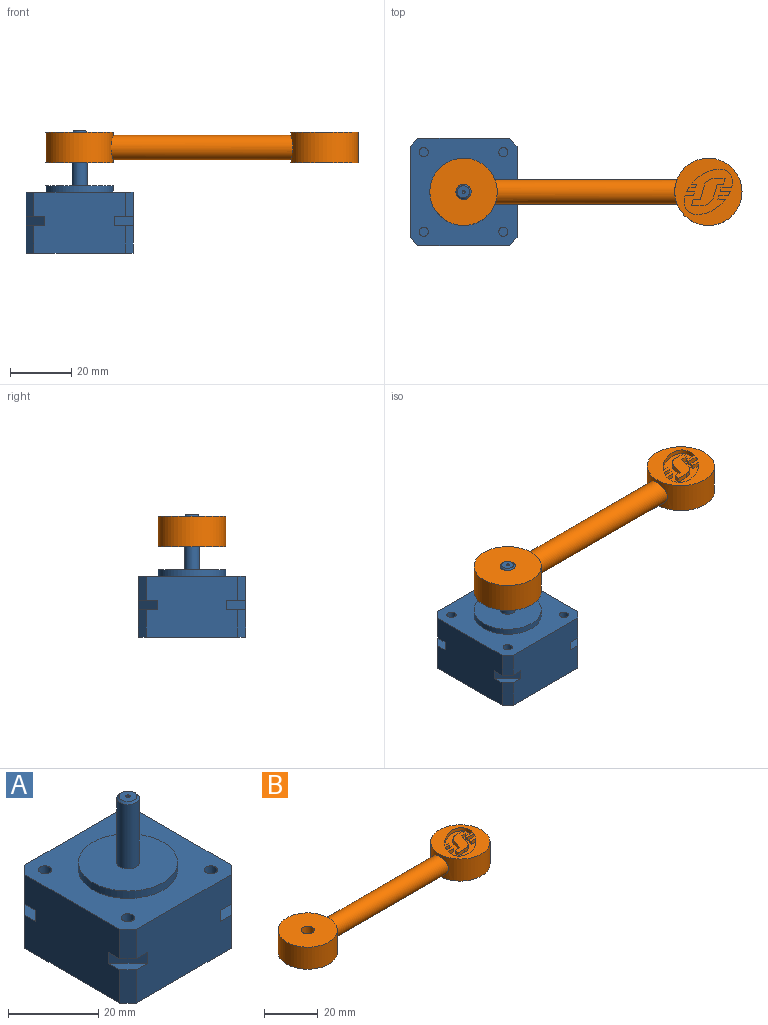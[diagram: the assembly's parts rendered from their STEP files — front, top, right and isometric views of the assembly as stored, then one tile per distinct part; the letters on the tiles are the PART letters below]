
ASSEMBLY  parts=2 mates=1
PART A: 41 faces, bbox 35x35x40 mm
  f0: plane 35x35mm, normal (0,0,1), area 803.1mm2, adj f1,f2,f3,f4,f13,f14,f15,f16
  f1: plane 29.8x20mm, normal (-1,0,0), area 575mm2, adj f0,f5,f8,f9,f10,f13,f16,f17
  f2: plane 29.8x20mm, normal (0,-1,0), area 575mm2, adj f0,f7,f8,f10,f11,f15,f16,f19
  f3: plane 29.8x20mm, normal (1,0,0), area 575mm2, adj f0,f6,f7,f11,f12,f14,f15,f18
  f4: plane 29.8x20mm, normal (0,1,0), area 575mm2, adj f0,f5,f6,f9,f12,f13,f14,f17
  f5: plane 6.1x6.1mm, normal (-0.71,0.71,0), area 25.9mm2, adj f1,f4,f9,f17
  f6: plane 6.1x6.1mm, normal (0.71,0.71,0), area 25.9mm2, adj f3,f4,f12,f18
  f7: plane 6.1x6.1mm, normal (0.71,-0.71,0), area 25.9mm2, adj f2,f3,f11,f19
  f8: plane 6.1x6.1mm, normal (-0.71,-0.71,0), area 25.9mm2, adj f1,f2,f10,f20
  f9: plane 6.1x6.1mm, normal (0,0,-1), area 15.2mm2, adj f1,f4,f5,f13
  f10: plane 6.1x6.1mm, normal (0,0,-1), area 15.2mm2, adj f1,f2,f8,f16
  f11: plane 6.1x6.1mm, normal (0,0,-1), area 15.2mm2, adj f2,f3,f7,f15
  f12: plane 6.1x6.1mm, normal (0,0,-1), area 15.2mm2, adj f3,f4,f6,f14
  f13: plane 8x2.6mm, normal (-0.71,0.71,0), area 29.4mm2, adj f0,f1,f4,f9
  f14: plane 8x2.6mm, normal (0.71,0.71,0), area 29.4mm2, adj f0,f3,f4,f12
  f15: plane 8x2.6mm, normal (0.71,-0.71,0), area 29.4mm2, adj f0,f2,f3,f11
  f16: plane 8x2.6mm, normal (-0.71,-0.71,0), area 29.4mm2, adj f0,f1,f2,f10
  f17: plane 6.1x6.1mm, normal (0,0,1), area 15.2mm2, adj f1,f4,f5,f23
  f18: plane 6.1x6.1mm, normal (0,0,1), area 15.2mm2, adj f3,f4,f6,f24
  f19: plane 6.1x6.1mm, normal (0,0,1), area 15.2mm2, adj f2,f3,f7,f21
  f20: plane 6.1x6.1mm, normal (0,0,1), area 15.2mm2, adj f1,f2,f8,f22
  f21: plane 9x2.6mm, normal (0.71,-0.71,0), area 33.1mm2, adj f2,f3,f19,f25
  f22: plane 9x2.6mm, normal (-0.71,-0.71,0), area 33.1mm2, adj f1,f2,f20,f25
  f23: plane 9x2.6mm, normal (-0.71,0.71,0), area 33.1mm2, adj f1,f4,f17,f25
  f24: plane 9x2.6mm, normal (0.71,0.71,0), area 33.1mm2, adj f3,f4,f18,f25
  f25: plane 35x35mm, normal (0,0,-1), area 1211.5mm2, adj f1,f2,f3,f4,f21,f22,f23,f24
  f26: cylinder r=11mm len=22mm, axis (0,0,-1), area 138.2mm2, adj f0,f27
  f27: plane 22x22mm, normal (0,0,1), area 360.5mm2, adj f26,f28
  f28: cylinder r=2.5mm len=17.5mm, axis (0,0,-1), area 274.9mm2, adj f27,f38
  f29: plane 4x4mm, normal (0,0,1), area 11.8mm2, adj f38,f39
  f30: cylinder r=1.5mm len=6mm, axis (0,0,1), area 56.5mm2, adj f0,f31
  f31: plane 3x3mm, normal (0,0,1), area 7.1mm2, adj f30
  f32: cylinder r=1.5mm len=6mm, axis (0,0,1), area 56.5mm2, adj f0,f33
  f33: plane 3x3mm, normal (0,0,1), area 7.1mm2, adj f32
  f34: cylinder r=1.5mm len=6mm, axis (0,0,1), area 56.5mm2, adj f0,f35
  f35: plane 3x3mm, normal (0,0,1), area 7.1mm2, adj f34
  f36: cylinder r=1.5mm len=6mm, axis (0,0,1), area 56.5mm2, adj f0,f37
  f37: plane 3x3mm, normal (0,0,1), area 7.1mm2, adj f36
  f38: cone r=2mm half-angle=45deg, axis (0,0,-1), area 10mm2, adj f28,f29
  f39: cylinder r=0.5mm len=3mm, axis (0,0,1), area 9.4mm2, adj f29,f40
  f40: cone r=0mm half-angle=59deg, axis (0,0,1), area 0.9mm2, adj f39
PART B: 36 faces, bbox 102x22x10 mm
  f0: extruded ~1.5x1.29mm, area 2.2mm2, adj f9,f13,f14,f24
  f1: extruded ~13.49x6.23mm, area 29.4mm2, adj f9,f16,f17,f24
  f2: extruded ~1.5x1.35mm, area 2.3mm2, adj f9,f19,f20,f24
  f3: extruded ~13.46x6.12mm, area 29.2mm2, adj f9,f22,f23,f24
  f4: cylinder r=11mm len=22mm, axis (0,0,-1), area 640.1mm2, adj f6,f7,f11
  f5: cylinder r=2.45mm len=10mm, axis (0,0,-1), area 153.9mm2, adj f6,f7
  f6: plane 22x22mm, normal (0,0,1), area 361.3mm2, adj f4,f5
  f7: plane 22x22mm, normal (0,0,-1), area 361.3mm2, adj f4,f5
  f8: cylinder r=11mm len=22mm, axis (0,0,-1), area 640.1mm2, adj f9,f10,f11
  f9: plane 22x22mm, normal (0,0,1), area 227.2mm2, adj f0,f1,f2,f3,f8,f12,f13,f14
  f10: plane 22x22mm, normal (0,0,-1), area 380.1mm2, adj f8
  f11: cylinder r=4mm len=59.51mm, axis (-1,0,0), area 1476.4mm2, adj f4,f8
  f12: plane 1.5x1.19mm, normal (0.97,-0.26,0), area 1.8mm2, adj f9,f13,f23,f24
  f13: plane 2.27x1.5mm, normal (0,-1,0), area 3.4mm2, adj f0,f9,f12,f24
  f14: plane 2.62x1.5mm, normal (0,1,0), area 3.9mm2, adj f0,f9,f15,f24
  f15: plane 1.5x1.19mm, normal (0.97,-0.26,0), area 1.8mm2, adj f9,f14,f16,f24
  f16: plane 2.75x1.5mm, normal (0,-1,0), area 4.1mm2, adj f1,f9,f15,f24
  f17: plane 2.45x1.5mm, normal (0,-1,0), area 3.7mm2, adj f1,f9,f18,f24
  f18: plane 1.5x1.19mm, normal (-0.97,0.25,0), area 1.8mm2, adj f9,f17,f19,f24
  f19: plane 2.98x1.5mm, normal (0,1,0), area 4.5mm2, adj f2,f9,f18,f24
  f20: plane 3.35x1.5mm, normal (0,-1,0), area 5mm2, adj f2,f9,f21,f24
  f21: plane 1.5x1.19mm, normal (-0.97,0.25,0), area 1.8mm2, adj f9,f20,f22,f24
  f22: plane 3.48x1.5mm, normal (0,1,0), area 5.2mm2, adj f3,f9,f21,f24
  f23: plane 1.75x1.5mm, normal (0,1,0), area 2.6mm2, adj f3,f9,f12,f24
  f24: plane 15.78x14.84mm, normal (0,0,1), area 111mm2, adj f0,f1,f2,f3,f12,f13,f14,f15
  f25: plane 11.03x8.77mm, normal (0,0,1), area 41.9mm2, adj f26,f27,f28,f29,f30,f31,f32,f33
  f26: cylinder r=3.46mm len=3.32mm, axis (0,0,1), area 6.7mm2, adj f24,f25,f27,f35
  f27: plane 4.25x1.5mm, normal (-0.96,0.28,0), area 6.6mm2, adj f24,f25,f26,f28
  f28: plane 2.31x1.5mm, normal (0,1,0), area 3.5mm2, adj f24,f25,f27,f29
  f29: plane 2.02x1.5mm, normal (-0.96,0.28,0), area 3.2mm2, adj f24,f25,f28,f30
  f30: plane 3.53x1.5mm, normal (0,-1,0), area 5.3mm2, adj f24,f25,f29,f31
  f31: cylinder r=3.89mm len=3.74mm, axis (0,0,1), area 7.5mm2, adj f24,f25,f30,f32
  f32: plane 4.12x1.5mm, normal (0.96,-0.28,0), area 6.4mm2, adj f24,f25,f31,f33
  f33: plane 2.04x1.5mm, normal (0,-1,0), area 3.1mm2, adj f24,f25,f32,f34
  f34: plane 1.84x1.5mm, normal (0.96,-0.28,0), area 2.9mm2, adj f24,f25,f33,f35
  f35: plane 3.59x1.5mm, normal (0,1,0), area 5.4mm2, adj f24,f25,f26,f34
PLACE A t=(-23.82,-27.77,-30.54)mm
PLACE B t=(-23.82,-27.77,-11.54)mm
MATE slider B.f4 <-> A.f26  axis (0,0,1) through (-23.82,-27.77,-1.54)mm
